# Revit family: logis_single_lever_bidet_mixer_70_with_metal_pop_up_waste_set_71203000
name_source: partatom
category: Plumbing Fixtures
revit_build: Autodesk Revit 2015 (Build: 20140903_1530(x64)
units: mm (PartAtom-declared; Revit-internal decimal feet)

## types (1)
- Chrome 000
    BIMobject category = Taps & Mixers
    BOSUseNativeGeometries = 1
    Brand url = http://www.hansgrohe-int.com
    Default Elevation = 4' - 0"
    Design country = Germany
    EAN code = https://4059625076873
    Edition number = 1
    IFC Classification = Sanitary Terminal
    Installation instructions = https://pro.hansgrohe-int.com
    Manufacturer country = Germany
    Manufacturer name = hansgrohe
    Masterformat 2014 Code = 10 28 16
    Masterformat 2014 Description = Bath Accessories
    Material main = Chrome
    NBS Reference Code = 94-94-xx
    NBS Reference Description = Thermostatic Mixing Valves
    Nominal height = 0
    Nominal width = 0
    OmniClass Code = 23-27 31 29 15
    OmniClass Description = Thermostatically Controlled Mixing Valves
    Product Guid = 4706ea06-7dd3-466d-8965-ac913ee40b48
    Product SKU = 71203000
    Product data url = https://bimobject.com
    Product family = Logis
    Product group = Bidet mixers
    Product name = Logis Single lever bidet mixer 70 with metal pop-up waste set 71203000
    Product url = https://pro.hansgrohe-int.com
    QR code = http://bimobject.com
    Technical description = https://pro.hansgrohe-int.com
    UNSPSC Code = 301815
    Uniclass 1.4 Code = L725111
    Uniclass 1.4 Description = Mixer taps
    Uniclass 2.0 Code = PR-94-94-xx
    Uniclass 2.0 Description = Thermostatic Mixing Valves
    Uniclass 2015 Code = Pr_40_20_87_09
    Uniclass 2015 Name = Bath taps
    Uniformat II Code = D2090
    Uniformat II Description = Other Plumbing Systems
    Weight Net (Kg) = 0

## geometry (parser evidence)
native form markers: Sweep x2
no freeform markers — native parametric forms only
